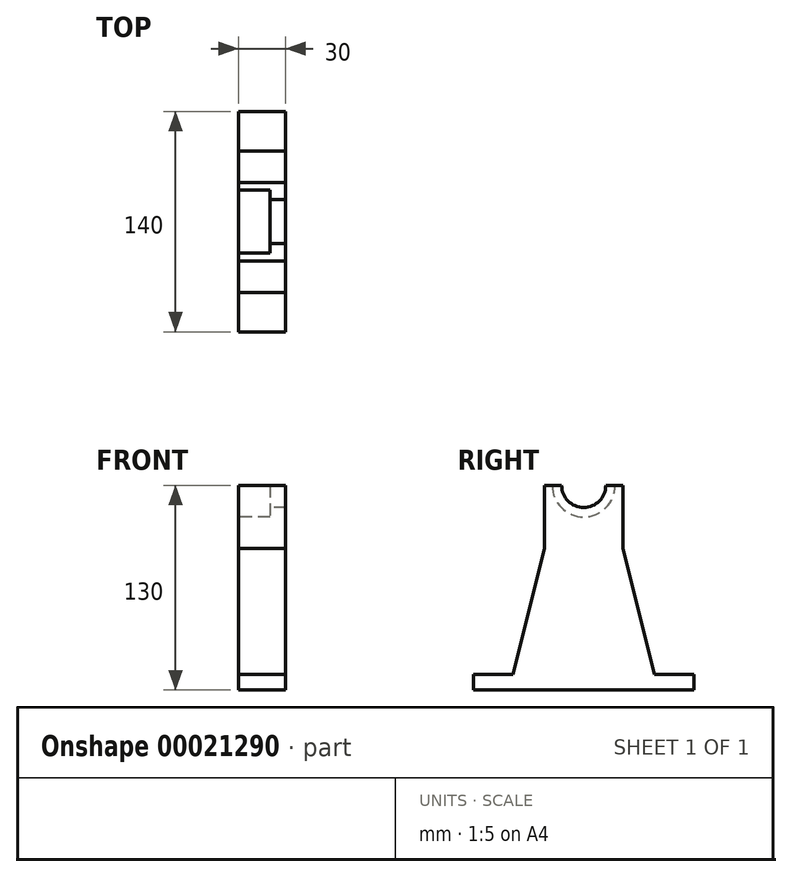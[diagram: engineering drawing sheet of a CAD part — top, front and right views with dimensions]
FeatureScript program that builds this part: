
annotation { "Feature Type Name" : "Feature", "Feature Type Description" : "" }
export const myFeature = defineFeature(function(context is Context, id is Id, definition is map)
    precondition{}
    {
        {
            var Q0;
            Q0=qCreatedBy(makeId("Right.planeOp"),FACE);
            var sketch = newSketch(context, id + "F0", { "sketchPlane" : qUnion([Q0])});
            skLineSegment(sketch, "E0", {"start": v(0, 0) * mm, "end": v(70, 0) * mm});
            skLineSegment(sketch, "E1", {"start": v(0, 90) * mm, "end": v(0, 0) * mm, "construction": true});
            skLineSegment(sketch, "E2.MirrorCS", {"start": v(0, 0) * mm, "end": v(-70, 0) * mm});
            skLineSegment(sketch, "E3", {"start": v(70, 0) * mm, "end": v(70, 10) * mm});
            skLineSegment(sketch, "E4.MirrorCS", {"start": v(-70, 0) * mm, "end": v(-70, 10) * mm});
            skLineSegment(sketch, "E5", {"start": v(70, 10) * mm, "end": v(45, 10) * mm});
            skLineSegment(sketch, "E6.MirrorCS", {"start": v(-70, 10) * mm, "end": v(-45, 10) * mm});
            skLineSegment(sketch, "E7", {"start": v(25, 90) * mm, "end": v(45, 10) * mm});
            skLineSegment(sketch, "E8.MirrorCS", {"start": v(-25, 90) * mm, "end": v(-45, 10) * mm});
            skLineSegment(sketch, "E9", {"start": v(25, 90) * mm, "end": v(25, 130) * mm});
            skLineSegment(sketch, "E10", {"start": v(25, 130) * mm, "end": v(20, 130) * mm});
            skLineSegment(sketch, "E11", {"start": v(-25, 90) * mm, "end": v(-25, 130) * mm});
            skLineSegment(sketch, "E12", {"start": v(-25, 130) * mm, "end": v(-20, 130) * mm});
            skArc(sketch, "E13", {"start": v(-20, 130) * mm, "mid": v(0, 110) * mm, "end": v(20, 130) * mm});
            skArc(sketch, "E14", {"start": v(14, 130) * mm, "mid": v(0, 116) * mm, "end": v(-14, 130) * mm});
            skLineSegment(sketch, "E15", {"start": v(20, 130) * mm, "end": v(14, 130) * mm});
            skLineSegment(sketch, "E16", {"start": v(-14, 130) * mm, "end": v(-20, 130) * mm});
            skSolve(sketch);
        }
        {
            var Q0;
            Q0 = qSketchRegion(id + "F0", true);
            extrude(context, id + "F1", {"entities" : qUnion([Q0]), "depth" : 30 * mm});
        }
        {
            var Q0;
            Q0=makeQuery(id+"F0.imprint","IMPRINT",FACE,{"disambiguationData":[TD([[makeQuery(id+"F0.imprint","IMPRINT",EDGE,{"derivedFrom":sQuery(id+"F0.wireOp",EDGE,"E0")}),1.0]])]});
            var sketch = newSketch(context, id + "F2", { "sketchPlane" : qUnion([Q0])});
            skCircle(sketch, "E17", {"center": v(0, 130) * mm, "radius": 20 * mm});
            skSolve(sketch);
        }
        {
            var Q0;
            Q0 = qSketchRegion(id + "F2", true);
            extrude(context, id + "F3", {"entities" : qUnion([Q0]), "operationType" : NewBodyOperationType.REMOVE, "depth" : 20 * mm});
        }
    });
